# Revit family: Sink-Vessel-Lavatory-KOHLER-CARILLON-K-96118T-1
name_source: partatom
category: Plumbing Fixtures
revit_build: Autodesk Revit 2017 (Build: 20160225_1515(x64)
units: mm (PartAtom-declared; Revit-internal decimal feet)

## family parameters
Cut with Voids When Loaded = No
Host = Face
OmniClass Number = 23.31.13.00
Part Type = Normal
Room Calculation Point = No
Round Connector Dimension = Use Diameter
Shared = No

## types (3) — shared parameters
ADA Compliant = No
Assembly Code = D2010400
CW Connection = No
Cold Water Inlet = Cold Water Inlet
Date Modified = 04/08/2021
Default Elevation = 36"
Description = Round Fashion Bowl
Drain Included = No
HW Connection = No
Height = 6 9/16"
Hot Water Inlet = Hot Water Inlet
Length = 17 3/8"
Manufacturer = KOHLER Co.
Master Format 2014 = 22 41 16
Master Format 2014 Name = Residential Lavatories and Sinks
Material = Vetreous China
Product Documentation Link = https://files.kohler.com.cn
Product Name = CARILLON
Product Page URL = https://www.kohler.com.cn
URL = http://www.kohler.com.cn
Vent Connection = No
Waste Connection = Yes
Waste Water Outlet = Waste Water Outlet
WaterSense Certified = No
Width = 17 3/8"

## per-type parameters (varying)
| type | Finish | Model | Type |
| 0- White | Kohler-Vitreous_China-0-White | K-96118T-0 | 1 |
| G81- Ice White | Kohler-Vitreous_China-G81-Ice_White | K-96118T-G81 | 2 |
| HB1- Matte Black | Kohler-Vitreous_China-HB1-Matte_Black | K-96118T-HB1 | 3 |

## geometry (parser evidence)
native form markers: Sweep x5
no freeform markers — native parametric forms only
